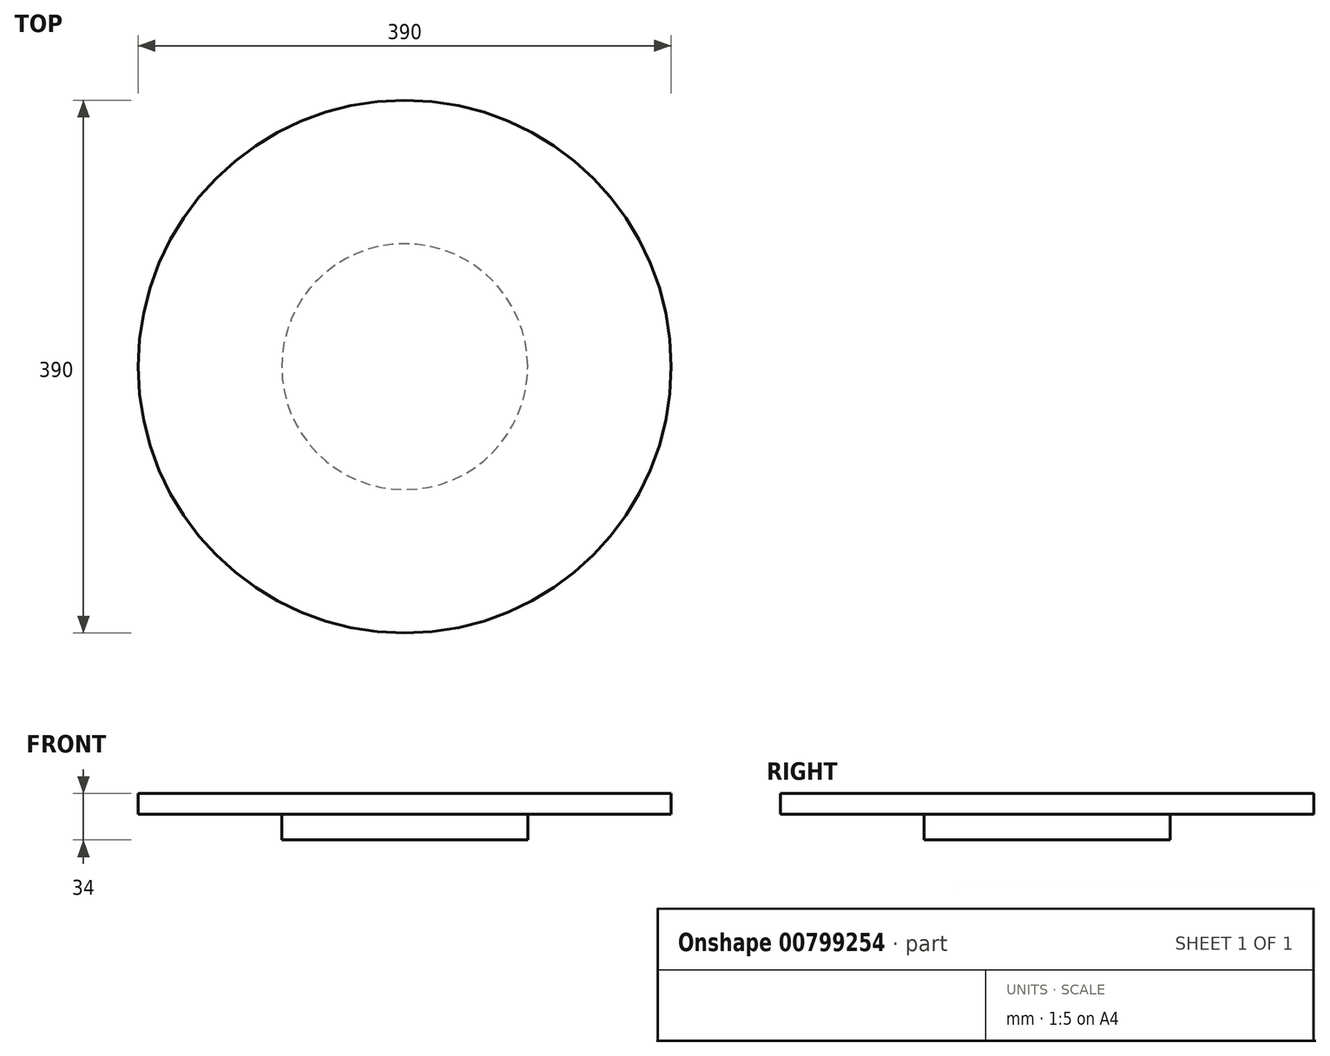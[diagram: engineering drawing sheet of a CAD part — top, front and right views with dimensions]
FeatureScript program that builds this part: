
annotation { "Feature Type Name" : "Feature", "Feature Type Description" : "" }
export const myFeature = defineFeature(function(context is Context, id is Id, definition is map)
    precondition{}
    {
        {
            assignVariable(context, id + "F0", {"name" : "base_thickness", "anyValue" : 19});
        }
        {
            assignVariable(context, id + "F1", {"name" : "plate_thickness", "anyValue" : 15});
        }
        {
            var Q0;
            Q0=qCreatedBy(makeId("Top.planeOp"),FACE);
            var sketch = newSketch(context, id + "F2", { "sketchPlane" : qUnion([Q0])});
            skCircle(sketch, "E0", {"center": v(0, 0) * mm, "radius": 90 * mm});
            skCircle(sketch, "E1", {"center": v(0, 0) * mm, "radius": 195 * mm});
            skSolve(sketch);
        }
        {
            var Q0;
            Q0=makeQuery(id+"F2.imprint","IMPRINT",FACE,{"disambiguationData":[TD([[makeQuery(id+"F2.imprint","IMPRINT",EDGE,{"derivedFrom":sQuery(id+"F2.wireOp",EDGE,"E0")}),1.0]])]});
            extrude(context, id + "F3", {"entities" : qUnion([Q0]), "depth" : (getVariable(context, 'base_thickness') + getVariable(context, 'plate_thickness')) * mm, "offsetDistance" : 25 * mm});
        }
        {
            var Q0;
            Q0=makeQuery(id+"F2.imprint","IMPRINT",FACE,{"disambiguationData":[TD([[makeQuery(id+"F2.imprint","IMPRINT",EDGE,{"derivedFrom":sQuery(id+"F2.wireOp",EDGE,"E0")}),-1.0]])]});
            extrude(context, id + "F4", {"entities" : qUnion([Q0]), "operationType" : NewBodyOperationType.ADD, "depth" : (getVariable(context, 'base_thickness') + getVariable(context, 'plate_thickness')) * mm, "offsetDistance" : 25 * mm, "hasSecondDirection" : true, "secondDirectionOppositeDirection" : false, "secondDirectionDepth" : (getVariable(context, 'base_thickness')) * mm});
        }
    });
